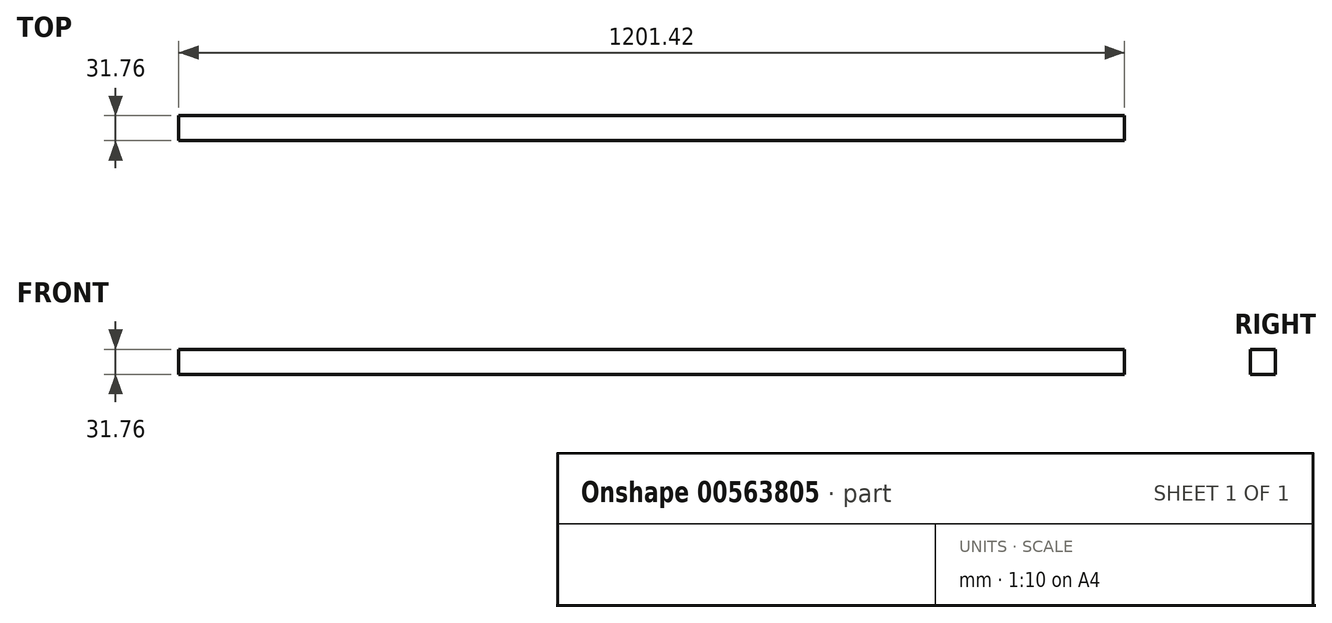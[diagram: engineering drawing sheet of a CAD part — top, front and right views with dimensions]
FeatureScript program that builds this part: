
annotation { "Feature Type Name" : "Feature", "Feature Type Description" : "" }
export const myFeature = defineFeature(function(context is Context, id is Id, definition is map)
    precondition{}
    {
        {
            var Q0;
            Q0=qCreatedBy(makeId("Top.planeOp"),FACE);
            var sketch = newSketch(context, id + "F0", { "sketchPlane" : qUnion([Q0])});
            skLineSegment(sketch, "E0.bottom", {"start": v(-600.7, 15.88) * mm, "end": v(600.7, 15.88) * mm});
            skLineSegment(sketch, "E0.top", {"start": v(-600.7, -15.88) * mm, "end": v(600.7, -15.88) * mm});
            skLineSegment(sketch, "E0.left", {"start": v(-600.7, 15.88) * mm, "end": v(-600.7, -15.88) * mm});
            skLineSegment(sketch, "E0.right", {"start": v(600.7, 15.88) * mm, "end": v(600.7, -15.88) * mm});
            skPoint(sketch, "E0.middle", {"position": v(0, 0) * mm});
            skSolve(sketch);
        }
        {
            var Q0;
            Q0=makeQuery(id+"F0.imprint","IMPRINT",FACE,{"disambiguationData":[TD([[makeQuery(id+"F0.imprint","IMPRINT",EDGE,{"derivedFrom":sQuery(id+"F0.wireOp",EDGE,"E0.bottom")}),-1.0]])]});
            extrude(context, id + "F1", {"entities" : qUnion([Q0]), "endBound" : BoundingType.SYMMETRIC, "depth" : 31.75 * mm, "offsetDistance" : 25.4 * mm});
        }
    });
